# Revit family: OKA-W, Kanaleinheit, blind, rastend, Höhe 100-150mm
name_source: partatom
category: Generic Models
revit_build: Autodesk Revit 2015 (Build: 20140606_1530(x64)
units: mm (PartAtom-declared; Revit-internal decimal feet)

## types (5) — shared parameters
Manufacturer = OBO Bettermann
Material = Steel, Galvanized
URL = http://www.obo-bettermann.com

## per-type parameters (varying)
| type | GTIN | Manufacturer Art. No. | Width |
| OKA-W20010050R | 4012195244479 | 7424500 | 200 mm  [stored 0.656168 ft] |
| OKA-W30010050R | 4012195244486 | 7424502 | 300 mm  [stored 0.984252 ft] |
| OKA-W40010050R | 4012195244493 | 7424504 | 400 mm  [stored 1.31234 ft] |
| OKA-W50010050R | 4012195244509 | 7424506 | 500 mm  [stored 1.64042 ft] |
| OKA-W60010050R | 4012195244516 | 7424508 | 600 mm |

note: column(s) folded — value = type name in every type: Article Type

note: [stored X ft] marks values corroborated as IEEE doubles in the binary element streams (Revit-internal decimal feet)

## geometry (parser evidence)
native form markers: Sweep x2
no freeform markers — native parametric forms only
